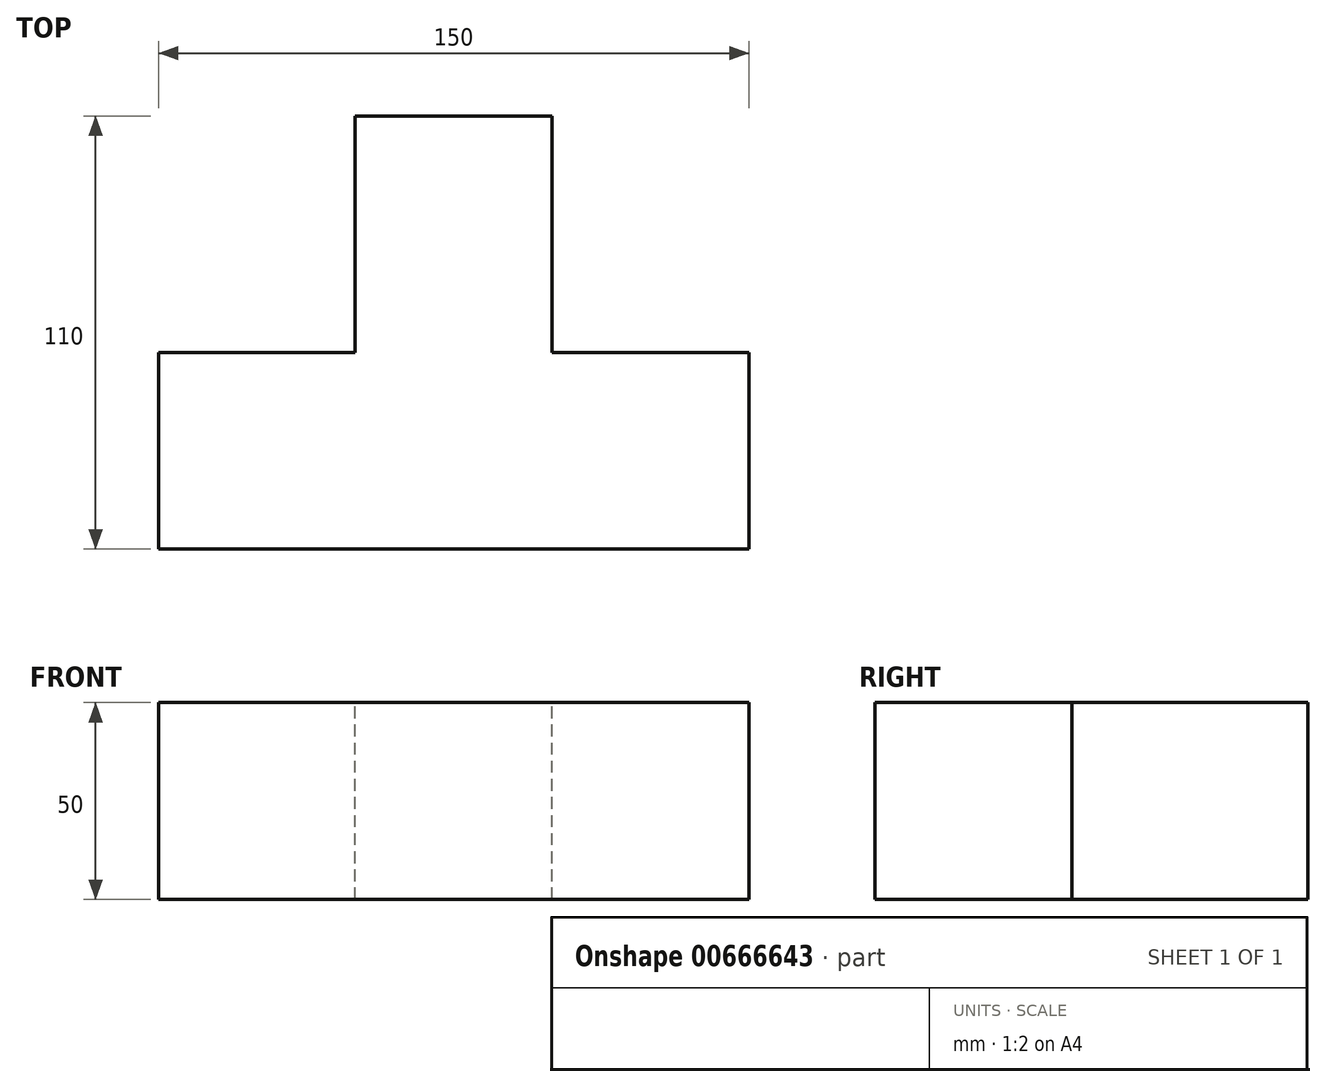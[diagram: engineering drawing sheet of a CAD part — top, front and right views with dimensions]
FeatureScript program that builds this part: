
annotation { "Feature Type Name" : "Feature", "Feature Type Description" : "" }
export const myFeature = defineFeature(function(context is Context, id is Id, definition is map)
    precondition{}
    {
        {
            var Q0;
            Q0=qCreatedBy(makeId("Top.planeOp"),FACE);
            var sketch = newSketch(context, id + "F0", { "sketchPlane" : qUnion([Q0])});
            skLineSegment(sketch, "E0.bottom", {"start": v(-77.48, 0) * mm, "end": v(72.52, 0) * mm});
            skLineSegment(sketch, "E0.top", {"start": v(-77.48, -50) * mm, "end": v(72.52, -50) * mm});
            skLineSegment(sketch, "E0.left", {"start": v(-77.48, 0) * mm, "end": v(-77.48, -50) * mm});
            skLineSegment(sketch, "E0.right", {"start": v(72.52, 0) * mm, "end": v(72.52, -50) * mm});
            skSolve(sketch);
        }
        {
            var Q0;
            Q0=makeQuery(id+"F0.imprint","IMPRINT",FACE,{"disambiguationData":[TD([[makeQuery(id+"F0.imprint","IMPRINT",EDGE,{"derivedFrom":sQuery(id+"F0.wireOp",EDGE,"E0.bottom")}),-1.0]])]});
            extrude(context, id + "F1", {"entities" : qUnion([Q0]), "depth" : 50 * mm, "offsetDistance" : 25 * mm});
        }
        {
            var Q0;
            Q0=makeQuery(id+"F1.opExtrude","SWEPT_FACE",FACE,{"disambiguationData":[OSD([sQuery(id+"F0.wireOp",EDGE,"E0.bottom")])]});
            var sketch = newSketch(context, id + "F2", { "sketchPlane" : qUnion([Q0])});
            skLineSegment(sketch, "E1", {"start": v(77.48, 0) * mm, "end": v(27.48, 0) * mm});
            skLineSegment(sketch, "E2.bottom", {"start": v(27.48, 0) * mm, "end": v(-22.52, 0) * mm});
            skLineSegment(sketch, "E2.top", {"start": v(27.48, 50) * mm, "end": v(-22.52, 50) * mm});
            skLineSegment(sketch, "E2.left", {"start": v(27.48, 0) * mm, "end": v(27.48, 50) * mm});
            skLineSegment(sketch, "E2.right", {"start": v(-22.52, 0) * mm, "end": v(-22.52, 50) * mm});
            skSolve(sketch);
        }
        {
            var Q0;
            Q0=makeQuery(id+"F2.imprint","IMPRINT",FACE,{"disambiguationData":[TD([[makeQuery(id+"F2.imprint","IMPRINT",EDGE,{"derivedFrom":sQuery(id+"F2.wireOp",EDGE,"E2.bottom")}),-1.0]])]});
            extrude(context, id + "F3", {"entities" : qUnion([Q0]), "operationType" : NewBodyOperationType.ADD, "depth" : 60 * mm, "offsetDistance" : 25 * mm});
        }
    });
